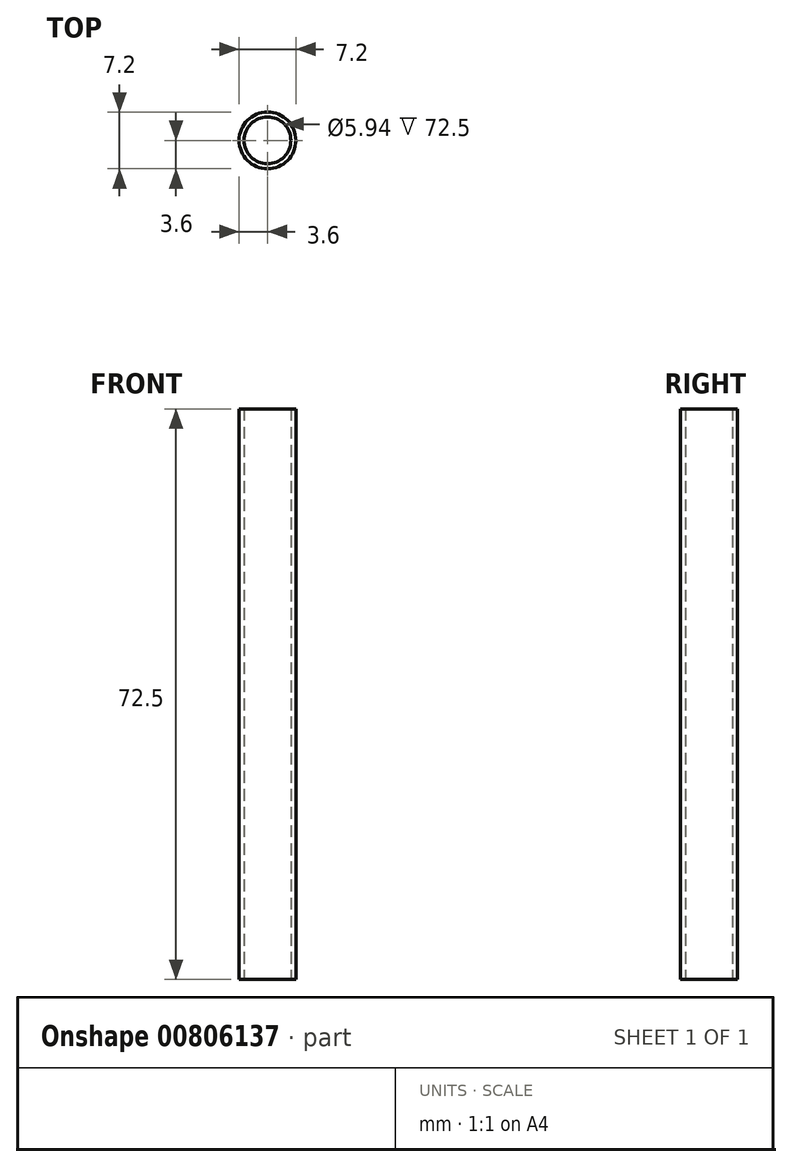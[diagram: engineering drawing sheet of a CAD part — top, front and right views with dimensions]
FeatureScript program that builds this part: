
annotation { "Feature Type Name" : "Feature", "Feature Type Description" : "" }
export const myFeature = defineFeature(function(context is Context, id is Id, definition is map)
    precondition{}
    {
        {
            var Q0;
            Q0=qCreatedBy(makeId("Top.planeOp"),FACE);
            var sketch = newSketch(context, id + "F0", { "sketchPlane" : qUnion([Q0])});
            skCircle(sketch, "E0", {"center": v(0, 0) * mm, "radius": 3.6 * mm});
            skCircle(sketch, "E1.0", {"center": v(0, 0) * mm, "radius": 2.97 * mm});
            skSolve(sketch);
        }
        {
            var Q0;
            Q0 = qSketchRegion(id + "F0", true);
            extrude(context, id + "F1", {"entities" : qUnion([Q0]), "depth" : 72.5 * mm, "offsetDistance" : 25 * mm});
        }
    });
